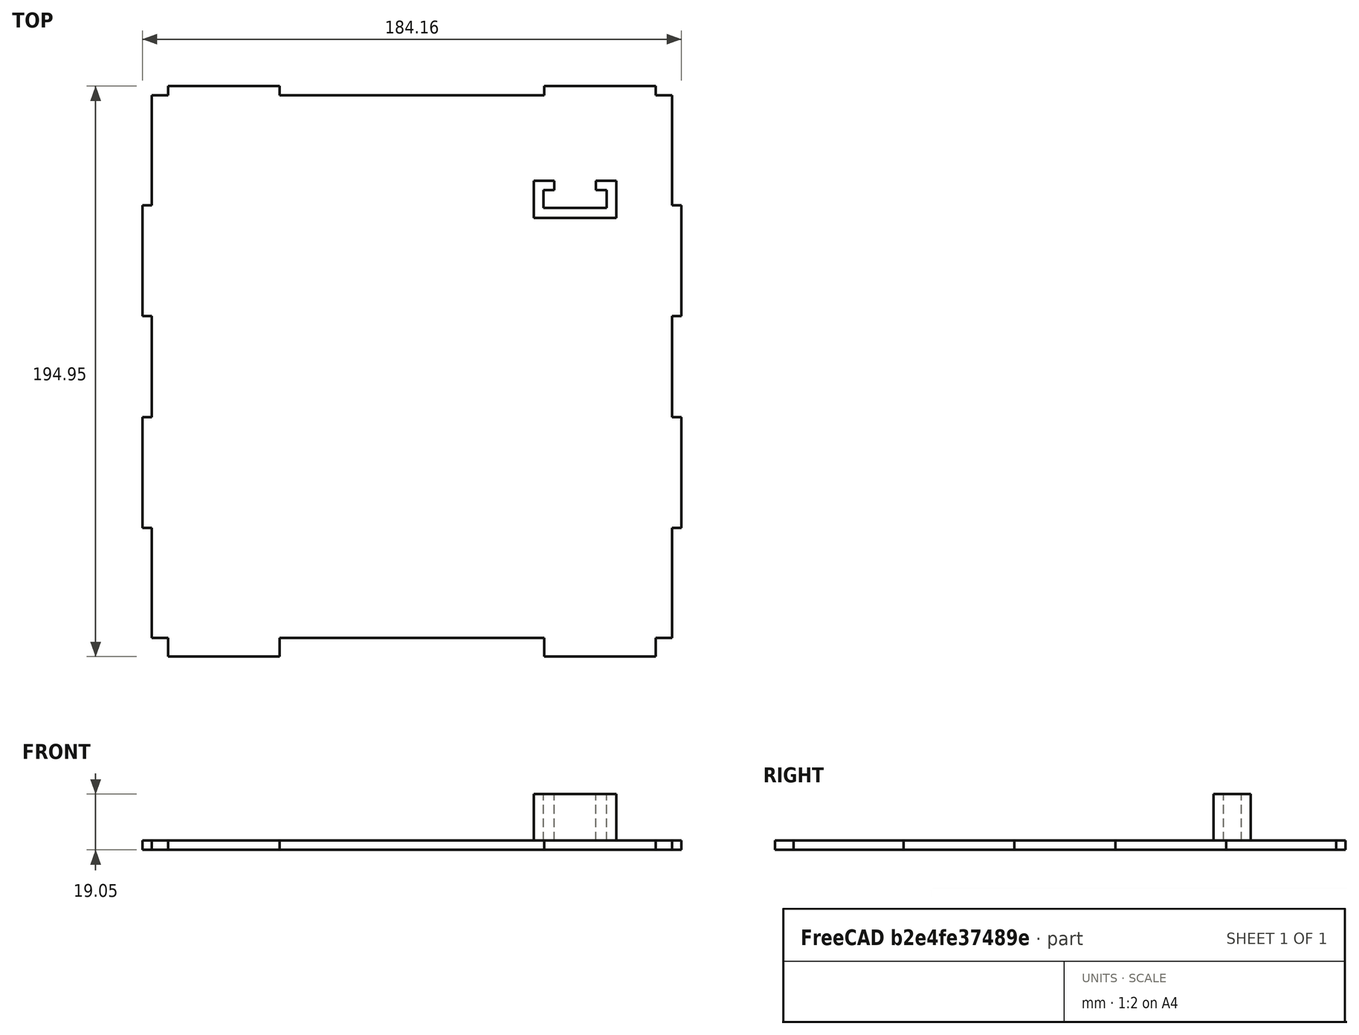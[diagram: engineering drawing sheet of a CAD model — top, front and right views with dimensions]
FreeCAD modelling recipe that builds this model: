
FCSTD DOCUMENT  (FreeCAD 0.18R4 (GitTag))
Label: lpr68k
License: All rights reserved
LicenseURL: http://en.wikipedia.org/wiki/All_rights_reserved
objects: Sketcher::SketchObject×2, PartDesign::Pad×2, PartDesign::Body×1, App::Part×1, Mesh::Feature×1
note: 7 computed .brp shape members not serialized (recipe doc carries the construction recipe); baked Part::Feature solids carry a one-line shape summary decoded from their .brp

FEATURE [Sketcher::SketchObject] Sketch
  MapMode = 5
  Support = -> [XY_Plane001]
  sketch-geometry (36):
    g0: LineSegment StartX=-88.9 StartY=92.71 StartZ=0 EndX=-83.312 EndY=92.71 EndZ=0
    g1: LineSegment StartX=-83.312 StartY=92.71 StartZ=0 EndX=-83.312 EndY=95.885 EndZ=0
    g2: LineSegment StartX=-83.312 StartY=95.885 StartZ=0 EndX=-45.212 EndY=95.885 EndZ=0
    g3: LineSegment StartX=-45.212 StartY=95.885 StartZ=0 EndX=-45.212 EndY=92.71 EndZ=0
    g4: LineSegment StartX=-45.212 StartY=92.71 StartZ=0 EndX=45.212 EndY=92.71 EndZ=0
    g5: LineSegment StartX=45.212 StartY=92.71 StartZ=0 EndX=45.212 EndY=95.885 EndZ=0
    g6: LineSegment StartX=45.212 StartY=95.885 StartZ=0 EndX=83.312 EndY=95.885 EndZ=0
    g7: LineSegment StartX=83.312 StartY=95.885 StartZ=0 EndX=83.312 EndY=92.71 EndZ=0
    g8: LineSegment StartX=83.312 StartY=92.71 StartZ=0 EndX=88.9 EndY=92.71 EndZ=0
    g9: LineSegment StartX=88.9 StartY=92.71 StartZ=0 EndX=88.9 EndY=55.118 EndZ=0
    g10: LineSegment StartX=88.9 StartY=55.118 StartZ=0 EndX=92.075 EndY=55.118 EndZ=0
    g11: LineSegment StartX=92.075 StartY=55.118 StartZ=0 EndX=92.075 EndY=17.272 EndZ=0
    g12: LineSegment StartX=92.075 StartY=17.272 StartZ=0 EndX=88.9 EndY=17.272 EndZ=0
    g13: LineSegment StartX=88.9 StartY=17.272 StartZ=0 EndX=88.9 EndY=-17.272 EndZ=0
    g14: LineSegment StartX=88.9 StartY=-17.272 StartZ=0 EndX=92.075 EndY=-17.272 EndZ=0
    g15: LineSegment StartX=92.075 StartY=-17.272 StartZ=0 EndX=92.075 EndY=-55.118 EndZ=0
    g16: LineSegment StartX=92.075 StartY=-55.118 StartZ=0 EndX=88.9 EndY=-55.118 EndZ=0
    g17: LineSegment StartX=88.9 StartY=-55.118 StartZ=0 EndX=88.9 EndY=-92.71 EndZ=0
    g18: LineSegment StartX=88.9 StartY=-92.71 StartZ=0 EndX=83.312 EndY=-92.71 EndZ=0
    g19: LineSegment StartX=83.312 StartY=-92.71 StartZ=0 EndX=83.312 EndY=-99.06 EndZ=0
    g20: LineSegment StartX=83.312 StartY=-99.06 StartZ=0 EndX=45.212 EndY=-99.06 EndZ=0
    g21: LineSegment StartX=45.212 StartY=-99.06 StartZ=0 EndX=45.212 EndY=-92.71 EndZ=0
    g22: LineSegment StartX=45.212 StartY=-92.71 StartZ=0 EndX=-45.212 EndY=-92.71 EndZ=0
    g23: LineSegment StartX=-45.212 StartY=-92.71 StartZ=0 EndX=-45.212 EndY=-99.06 EndZ=0
    g24: LineSegment StartX=-45.212 StartY=-99.06 StartZ=0 EndX=-83.312 EndY=-99.06 EndZ=0
    g25: LineSegment StartX=-83.312 StartY=-99.06 StartZ=0 EndX=-83.312 EndY=-92.71 EndZ=0
    g26: LineSegment StartX=-83.312 StartY=-92.71 StartZ=0 EndX=-88.9 EndY=-92.71 EndZ=0
    g27: LineSegment StartX=-88.9 StartY=-92.71 StartZ=0 EndX=-88.9 EndY=-55.118 EndZ=0
    g28: LineSegment StartX=-88.9 StartY=-55.118 StartZ=0 EndX=-92.075 EndY=-55.118 EndZ=0
    g29: LineSegment StartX=-92.075 StartY=-55.118 StartZ=0 EndX=-92.075 EndY=-17.272 EndZ=0
    g30: LineSegment StartX=-92.075 StartY=-17.272 StartZ=0 EndX=-88.9 EndY=-17.272 EndZ=0
    g31: LineSegment StartX=-88.9 StartY=-17.272 StartZ=0 EndX=-88.9 EndY=17.272 EndZ=0
    g32: LineSegment StartX=-88.9 StartY=17.272 StartZ=0 EndX=-92.075 EndY=17.272 EndZ=0
    g33: LineSegment StartX=-92.075 StartY=17.272 StartZ=0 EndX=-92.075 EndY=55.118 EndZ=0
    g34: LineSegment StartX=-92.075 StartY=55.118 StartZ=0 EndX=-88.9 EndY=55.118 EndZ=0
    g35: LineSegment StartX=-88.9 StartY=55.118 StartZ=0 EndX=-88.9 EndY=92.71 EndZ=0
  constraints (106):
    c: Horizontal(g0)
    c: Coincident(g0,g1)
    c: Vertical(g1)
    c: Coincident(g1,g2)
    c: Horizontal(g2)
    c: Coincident(g2,g3)
    c: Coincident(g3,g4)
    c: Coincident(g4,g5)
    c: Coincident(g5,g6)
    c: Horizontal(g6)
    c: Coincident(g6,g7)
    c: Coincident(g7,g8)
    c: Horizontal(g8)
    c: Coincident(g8,g9)
    c: Coincident(g9,g10)
    c: Coincident(g10,g11)
    c: Coincident(g11,g12)
    c: Coincident(g12,g13)
    c: Coincident(g13,g14)
    c: Coincident(g14,g15)
    c: Coincident(g15,g16)
    c: Coincident(g16,g17)
    c: Vertical(g17)
    c: Coincident(g17,g18)
    c: Coincident(g18,g19)
    c: Vertical(g19)
    c: Coincident(g19,g20)
    c: Horizontal(g20)
    c: Coincident(g20,g21)
    c: Coincident(g21,g22)
    c: Horizontal(g22)
    c: Coincident(g22,g23)
    c: Vertical(g23)
    c: Coincident(g23,g24)
    c: Horizontal(g24)
    c: Coincident(g24,g25)
    c: Vertical(g25)
    c: Coincident(g25,g26)
    c: Coincident(g26,g27)
    c: Vertical(g27)
    c: Coincident(g27,g28)
    c: Coincident(g28,g29)
    c: Coincident(g29,g30)
    c: Coincident(g30,g31)
    c: Coincident(g31,g32)
    c: Coincident(g32,g33)
    c: Coincident(g33,g34)
    c: Coincident(g34,g35)
    c: Coincident(g35,g0)
    c: Vertical(g3)
    c: Vertical(g5)
    c: Vertical(g7)
    c: Vertical(g35)
    c: Vertical(g29)
    c: Vertical(g33)
    c: Vertical(g9)
    c: Vertical(g11)
    c: Vertical(g13)
    c: Vertical(g15)
    c: Horizontal(g34)
    c: Horizontal(g32)
    c: Horizontal(g30)
    c: Horizontal(g28)
    c: Horizontal(g16)
    c: Horizontal(g14)
    c: Horizontal(g12)
    c: Horizontal(g10)
    c: Equal(g31,g13)
    c: Equal(g4,g22)
    c: Equal(g29,g33)
    c: Equal(g33,g11)
    c: Equal(g11,g15)
    c: Equal(g2,g6)
    c: Equal(g6,g20)
    c: Equal(g20,g24)
    c: Horizontal(g26)
    c: Horizontal(g18)
    c: Equal(g0,g8)
    c: Equal(g8,g26)
    c: Equal(g26,g18)
    c: Equal(g1,g3)
    c: Equal(g3,g5)
    c: Equal(g5,g7)
    c: Equal(g25,g23)
    c: Equal(g23,g21)
    c: Equal(g21,g19)
    c: Equal(g34,g32)
    c: Equal(g32,g30)
    c: Equal(g30,g28)
    c: Equal(g28,g10)
    c: Equal(g10,g12)
    c: Equal(g12,g14)
    c: Equal(g14,g16)
    c: Symmetric(g3,g4,g-2)
    c: Symmetric(g31,g30,g-1)
    c: DistanceX(g33,g34) = 3.175
    c: DistanceY(g0,g1) = 3.175
    c: DistanceY(g24,g25) = 6.35
    c: DistanceY(g32,g33) = 37.846
    c: Equal(g35,g9)
    c: Equal(g35,g27)
    c: DistanceX(g1,g2) = 38.1
    c: DistanceX(g3,g4) = 90.424
    c: DistanceY(g26,g27) = 37.592
    c: DistanceY(g-1,g0) = 92.71
    c: DistanceX(g31,g-1) = 88.9
FEATURE [Sketcher::SketchObject] Sketch001
  MapMode = 5
  Placement = pos=(0,0,3.175) rot=(0,0,1;0rad)
  sketch-geometry (12):
    g0: LineSegment StartX=48.641 StartY=63.5 StartZ=0 EndX=41.656 EndY=63.5 EndZ=0
    g1: LineSegment StartX=41.656 StartY=63.5 StartZ=0 EndX=41.656 EndY=50.8 EndZ=0
    g2: LineSegment StartX=41.656 StartY=50.8 StartZ=0 EndX=69.85 EndY=50.8 EndZ=0
    g3: LineSegment StartX=69.85 StartY=50.8 StartZ=0 EndX=69.85 EndY=63.5 EndZ=0
    g4: LineSegment StartX=69.85 StartY=63.5 StartZ=0 EndX=62.865 EndY=63.5 EndZ=0
    g5: LineSegment StartX=62.865 StartY=63.5 StartZ=0 EndX=62.865 EndY=60.325 EndZ=0
    g6: LineSegment StartX=62.865 StartY=60.325 StartZ=0 EndX=66.548 EndY=60.325 EndZ=0
    g7: LineSegment StartX=66.548 StartY=60.325 StartZ=0 EndX=66.548 EndY=54.229 EndZ=0
    g8: LineSegment StartX=66.548 StartY=54.229 StartZ=0 EndX=44.958 EndY=54.229 EndZ=0
    g9: LineSegment StartX=44.958 StartY=54.229 StartZ=0 EndX=44.958 EndY=60.325 EndZ=0
    g10: LineSegment StartX=44.958 StartY=60.325 StartZ=0 EndX=48.641 EndY=60.325 EndZ=0
    g11: LineSegment StartX=48.641 StartY=60.325 StartZ=0 EndX=48.641 EndY=63.5 EndZ=0
  constraints (36):
    c: Horizontal(g0)
    c: Coincident(g0,g1)
    c: Vertical(g1)
    c: Coincident(g1,g2)
    c: Horizontal(g2)
    c: Coincident(g2,g3)
    c: Vertical(g3)
    c: Coincident(g3,g4)
    c: Horizontal(g4)
    c: Coincident(g4,g5)
    c: Coincident(g5,g6)
    c: Coincident(g6,g7)
    c: Vertical(g7)
    c: Coincident(g7,g8)
    c: Horizontal(g8)
    c: Coincident(g8,g9)
    c: Vertical(g9)
    c: Coincident(g9,g10)
    c: Horizontal(g10)
    c: Coincident(g10,g11)
    c: Coincident(g11,g0)
    c: Vertical(g5)
    c: Vertical(g11)
    c: Horizontal(g6)
    c: Equal(g10,g6)
    c: Equal(g4,g0)
    c: Equal(g3,g1)
    c: Equal(g7,g9)
    c: DistanceX(g9,g10) = 3.683
    c: DistanceX(g8,g7) = 21.59
    c: DistanceY(g10,g0) = 3.175
    c: DistanceX(g0,g0) = 6.985
    c: DistanceY(g7,g6) = 6.096
    c: DistanceY(g2,g3) = 12.7
    c: DistanceX(g-1,g2) = 69.85
    c: DistanceY(g-1,g0) = 63.5
FEATURE [PartDesign::Pad] Pad
  Length = 3.175
  Length2 = 99.9998
  Profile = -> Sketch
  Type = 0
FEATURE [PartDesign::Pad] Pad001
  BaseFeature = -> Pad
  Length = 15.875
  Length2 = 99.9998
  Profile = -> Sketch001
  Type = 0
FEATURE [PartDesign::Body] Body
  Group = -> [Sketch,Sketch001,Pad,Pad001]
  Origin = -> Origin001
  Tip = -> Pad001
FEATURE [App::Part] Part
  Group = -> [Body]
  Origin = -> Origin
FEATURE [Mesh::Feature] Mesh  label="lpr68k"
